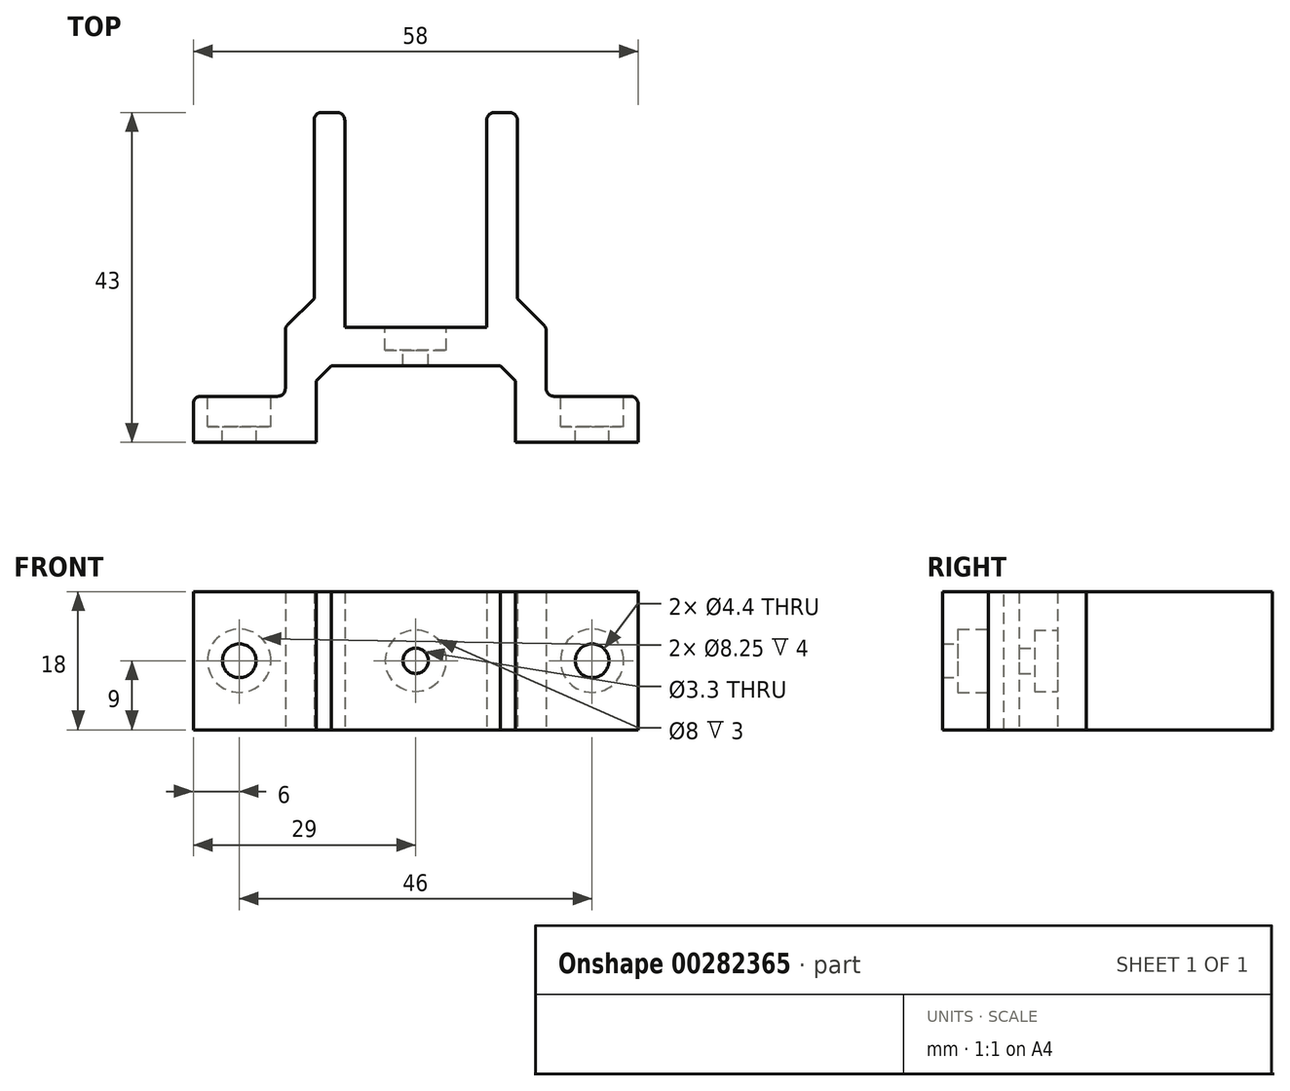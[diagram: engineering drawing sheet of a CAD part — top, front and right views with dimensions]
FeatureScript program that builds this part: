
annotation { "Feature Type Name" : "Feature", "Feature Type Description" : "" }
export const myFeature = defineFeature(function(context is Context, id is Id, definition is map)
    precondition{}
    {
        {
            var Q0;
            Q0=qCreatedBy(makeId("Top.planeOp"),FACE);
            var sketch = newSketch(context, id + "F0", { "sketchPlane" : qUnion([Q0])});
            skLineSegment(sketch, "E0", {"start": v(0, 0) * mm, "end": v(0, 6) * mm});
            skLineSegment(sketch, "E1", {"start": v(0, 6) * mm, "end": v(12, 6) * mm});
            skLineSegment(sketch, "E2", {"start": v(12, 6) * mm, "end": v(12, 15) * mm});
            skLineSegment(sketch, "E3", {"start": v(15.75, 43) * mm, "end": v(19.75, 43) * mm});
            skLineSegment(sketch, "E4", {"start": v(19.75, 43) * mm, "end": v(19.75, 15) * mm});
            skLineSegment(sketch, "E5", {"start": v(19.75, 15) * mm, "end": v(38.25, 15) * mm});
            skLineSegment(sketch, "E6", {"start": v(38.25, 15) * mm, "end": v(38.25, 43) * mm});
            skLineSegment(sketch, "E7", {"start": v(38.25, 43) * mm, "end": v(42.25, 43) * mm});
            skLineSegment(sketch, "E8", {"start": v(46, 15) * mm, "end": v(46, 6) * mm});
            skLineSegment(sketch, "E9", {"start": v(46, 6) * mm, "end": v(58, 6) * mm});
            skLineSegment(sketch, "E10", {"start": v(58, 6) * mm, "end": v(58, 0) * mm});
            skLineSegment(sketch, "E11", {"start": v(58, 0) * mm, "end": v(42, 0) * mm});
            skLineSegment(sketch, "E12.bottom", {"start": v(16, 10) * mm, "end": v(42, 10) * mm});
            skLineSegment(sketch, "E12.left", {"start": v(16, 10) * mm, "end": v(16, 0) * mm});
            skLineSegment(sketch, "E12.right", {"start": v(42, 10) * mm, "end": v(42, 0) * mm});
            skLineSegment(sketch, "E13.trimOffspring", {"start": v(16, 0) * mm, "end": v(0, 0) * mm});
            skLineSegment(sketch, "E14", {"start": v(29, 15) * mm, "end": v(29, 10) * mm, "construction": true});
            skLineSegment(sketch, "E15", {"start": v(12, 15) * mm, "end": v(15.75, 18.75) * mm});
            skLineSegment(sketch, "E16", {"start": v(15.75, 18.75) * mm, "end": v(15.75, 43) * mm});
            skLineSegment(sketch, "E17", {"start": v(46, 15) * mm, "end": v(42.25, 18.75) * mm});
            skLineSegment(sketch, "E18", {"start": v(42.25, 18.75) * mm, "end": v(42.25, 43) * mm});
            skSolve(sketch);
        }
        {
            var Q0;
            Q0 = qSketchRegion(id + "F0", true);
            extrude(context, id + "F1", {"entities" : qUnion([Q0]), "depth" : 18 * mm});
        }
        {
            var Q0;
            Q0=makeQuery(id+"F1.opExtrude","SWEPT_FACE",FACE,{"disambiguationData":[OSD([sQuery(id+"F0.wireOp",EDGE,"E9")])]});
            var sketch = newSketch(context, id + "F2", { "sketchPlane" : qUnion([Q0])});
            skLineSegment(sketch, "E19", {"start": v(-52, 18) * mm, "end": v(-52, 0) * mm, "construction": true});
            skPoint(sketch, "E20", {"position": v(-52, 9) * mm});
            skSolve(sketch);
        }
        {
            var Q0;
            Q0=makeQuery(id+"F1.opExtrude","SWEPT_FACE",FACE,{"disambiguationData":[OSD([sQuery(id+"F0.wireOp",EDGE,"E1")])]});
            var sketch = newSketch(context, id + "F3", { "sketchPlane" : qUnion([Q0])});
            skLineSegment(sketch, "E21", {"start": v(-6, 18) * mm, "end": v(-6, 0) * mm, "construction": true});
            skPoint(sketch, "E22", {"position": v(-6, 9) * mm});
            skSolve(sketch);
        }
        {
            var Q0;
            Q0=sQuery(id+"F2.wireOp",VERTEX,"E20");
            var Q1;
            Q1=sQuery(id+"F3.wireOp",VERTEX,"E22");
            var Q2;
            Q2=makeQuery(id+"F1.opExtrude","SWEPT_BODY",BODY,{"disambiguationData":[OSD([sQuery(id+"F0.wireOp",EDGE,"E0"),sQuery(id+"F0.wireOp",EDGE,"E1"),sQuery(id+"F0.wireOp",EDGE,"E2"),sQuery(id+"F0.wireOp",EDGE,"E3"),sQuery(id+"F0.wireOp",EDGE,"E4"),sQuery(id+"F0.wireOp",EDGE,"E5"),sQuery(id+"F0.wireOp",EDGE,"E6"),sQuery(id+"F0.wireOp",EDGE,"E7"),sQuery(id+"F0.wireOp",EDGE,"E8"),sQuery(id+"F0.wireOp",EDGE,"E9"),sQuery(id+"F0.wireOp",EDGE,"E10"),sQuery(id+"F0.wireOp",EDGE,"E11"),sQuery(id+"F0.wireOp",EDGE,"E12.bottom"),sQuery(id+"F0.wireOp",EDGE,"E12.left"),sQuery(id+"F0.wireOp",EDGE,"E12.right"),sQuery(id+"F0.wireOp",EDGE,"E13.trimOffspring")])]});
            hole(context, id + "F4", {"style" : HoleStyle.C_BORE, "endStyle" : HoleEndStyle.THROUGH, "standardTappedOrClearance" : lookupTablePath({ "standard" : "ISO", "fit" : "Normal", "size" : "M4", "type" : "Clearance" }), "standardBlindInLast" : lookupTablePath({ "fit" : "Standard", "standard" : "ISO", "size" : "M4", "type" : "Clearance" }), "holeDiameter" : 4.4 * mm, "cBoreDiameter" : 8.25 * mm, "cBoreDepth" : 4 * mm, "tappedDepth" : 3 * mm, "tapClearance" : 3, "startFromSketch" : true, "locations" : qUnion([Q0, Q1]), "scope" : qUnion([Q2])});
        }
        {
            var Q0;
            Q0=makeQuery(id+"F1.opExtrude","SWEPT_EDGE",EDGE,{"disambiguationData":[OSD([sQuery(id+"F0.wireOp",EDGE,"E12.bottom"),sQuery(id+"F0.wireOp",EDGE,"E12.left")])]});
            var Q1;
            Q1=makeQuery(id+"F1.opExtrude","SWEPT_EDGE",EDGE,{"disambiguationData":[OSD([sQuery(id+"F0.wireOp",EDGE,"E12.bottom"),sQuery(id+"F0.wireOp",EDGE,"E12.right")])]});
            chamfer(context, id + "F5", {"entities" : qUnion([Q0, Q1]), "width" : 2 * mm, "tangentPropagation" : true});
        }
        {
            var Q0;
            Q0=makeQuery(id+"F1.opExtrude","SWEPT_EDGE",EDGE,{"disambiguationData":[OSD([sQuery(id+"F0.wireOp",EDGE,"E8"),sQuery(id+"F0.wireOp",EDGE,"E9")])]});
            var Q1;
            Q1=makeQuery(id+"F1.opExtrude","SWEPT_EDGE",EDGE,{"disambiguationData":[OSD([sQuery(id+"F0.wireOp",EDGE,"E7"),sQuery(id+"F0.wireOp",EDGE,"E8")])]});
            var Q2;
            Q2=makeQuery(id+"F1.opExtrude","SWEPT_EDGE",EDGE,{"disambiguationData":[OSD([sQuery(id+"F0.wireOp",EDGE,"E6"),sQuery(id+"F0.wireOp",EDGE,"E7")])]});
            var Q3;
            Q3=makeQuery(id+"F1.opExtrude","SWEPT_EDGE",EDGE,{"disambiguationData":[OSD([sQuery(id+"F0.wireOp",EDGE,"E3"),sQuery(id+"F0.wireOp",EDGE,"E4")])]});
            var Q4;
            Q4=makeQuery(id+"F1.opExtrude","SWEPT_EDGE",EDGE,{"disambiguationData":[OSD([sQuery(id+"F0.wireOp",EDGE,"E2"),sQuery(id+"F0.wireOp",EDGE,"E3")])]});
            var Q5;
            Q5=makeQuery(id+"F1.opExtrude","SWEPT_EDGE",EDGE,{"disambiguationData":[OSD([sQuery(id+"F0.wireOp",EDGE,"E1"),sQuery(id+"F0.wireOp",EDGE,"E2")])]});
            var Q6;
            Q6=makeQuery(id+"F1.opExtrude","SWEPT_EDGE",EDGE,{"disambiguationData":[OSD([sQuery(id+"F0.wireOp",EDGE,"E0"),sQuery(id+"F0.wireOp",EDGE,"E1")])]});
            var Q7;
            Q7=makeQuery(id+"F1.opExtrude","SWEPT_EDGE",EDGE,{"disambiguationData":[OSD([sQuery(id+"F0.wireOp",EDGE,"E9"),sQuery(id+"F0.wireOp",EDGE,"E10")])]});
            fillet(context, id + "F6", {"entities" : qUnion([Q0, Q1, Q2, Q3, Q4, Q5, Q6, Q7]), "radius" : 1 * mm, "tangentPropagation" : true, "allowEdgeOverflow" : false});
        }
        {
            var Q0;
            Q0=makeQuery(id+"F1.opExtrude","SWEPT_FACE",FACE,{"disambiguationData":[OSD([sQuery(id+"F0.wireOp",EDGE,"E5")])]});
            var sketch = newSketch(context, id + "F7", { "sketchPlane" : qUnion([Q0])});
            skLineSegment(sketch, "E23", {"start": v(-29, 18) * mm, "end": v(-29, 0) * mm, "construction": true});
            skCircle(sketch, "E24", {"center": v(-29, 9) * mm, "radius": 1.65 * mm});
            skSolve(sketch);
        }
        {
            var Q0;
            Q0 = qSketchRegion(id + "F7", true);
            extrude(context, id + "F8", {"entities" : qUnion([Q0]), "operationType" : NewBodyOperationType.REMOVE, "endBound" : BoundingType.THROUGH_ALL, "oppositeDirection" : true, "depth" : 25 * mm});
        }
        {
            var Q0;
            Q0=makeQuery(id+"F1.opExtrude","SWEPT_FACE",FACE,{"disambiguationData":[OSD([sQuery(id+"F0.wireOp",EDGE,"E5")])]});
            var sketch = newSketch(context, id + "F9", { "sketchPlane" : qUnion([Q0])});
            skCircle(sketch, "E25", {"center": v(-29, 9) * mm, "radius": 4 * mm});
            skSolve(sketch);
        }
        {
            var Q0;
            Q0 = qSketchRegion(id + "F9", true);
            extrude(context, id + "F10", {"entities" : qUnion([Q0]), "operationType" : NewBodyOperationType.REMOVE, "oppositeDirection" : true, "depth" : 3 * mm});
        }
    });
